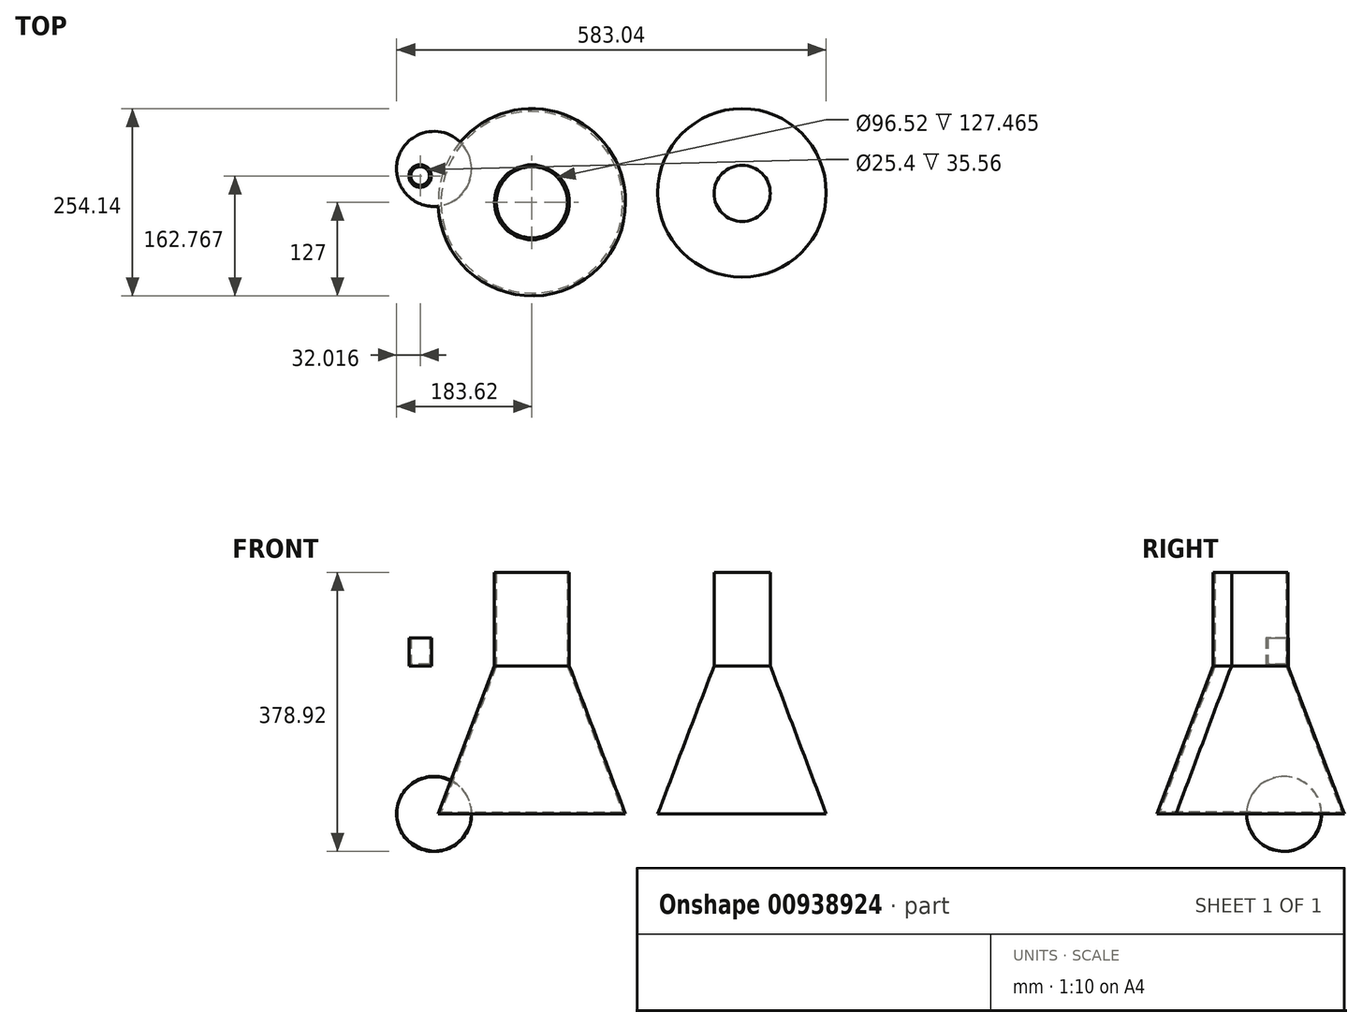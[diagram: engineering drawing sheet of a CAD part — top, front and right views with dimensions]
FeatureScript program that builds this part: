
annotation { "Feature Type Name" : "Feature", "Feature Type Description" : "" }
export const myFeature = defineFeature(function(context is Context, id is Id, definition is map)
    precondition{}
    {
        {
            var Q0;
            Q0=qCreatedBy(makeId("Top.planeOp"),FACE);
            var sketch = newSketch(context, id + "F0", { "sketchPlane" : qUnion([Q0])});
            skCircle(sketch, "E0", {"center": v(0, 0) * mm, "radius": 127 * mm});
            skSolve(sketch);
        }
        {
            var Q0;
            Q0=qCreatedBy(makeId("Top.planeOp"),FACE);
            cPlane(context, id + "F1", {"entities" : qUnion([Q0]), "cplaneType" : CPlaneType.OFFSET, "offset" : 200.9 * mm, "width" : 152.4 * mm, "height" : 152.4 * mm});
        }
        {
            var Q0;
            Q0=qCreatedBy(id+"F1.planeOp",FACE);
            var sketch = newSketch(context, id + "F2", { "sketchPlane" : qUnion([Q0])});
            skCircle(sketch, "E1", {"center": v(0, 0) * mm, "radius": 50.8 * mm});
            skSolve(sketch);
        }
        {
            var Q0;
            Q0=makeQuery(id+"F2.imprint","IMPRINT",FACE,{"disambiguationData":[TD([[makeQuery(id+"F2.imprint","IMPRINT",EDGE,{"derivedFrom":sQuery(id+"F2.wireOp",EDGE,"E1")}),1.0]])]});
            var sketch = newSketch(context, id + "F3", { "sketchPlane" : qUnion([Q0])});
            skCircle(sketch, "E2", {"center": v(0, 0) * mm, "radius": 19.15 * mm});
            skSolve(sketch);
        }
        {
            var Q0;
            Q0=makeQuery(id+"F0.imprint","IMPRINT",FACE,{"disambiguationData":[TD([[makeQuery(id+"F0.imprint","IMPRINT",EDGE,{"derivedFrom":sQuery(id+"F0.wireOp",EDGE,"E0")}),1.0]])]});
            var Q1;
            Q1=makeQuery(id+"F2.imprint","IMPRINT",FACE,{"disambiguationData":[TD([[makeQuery(id+"F2.imprint","IMPRINT",EDGE,{"derivedFrom":sQuery(id+"F2.wireOp",EDGE,"E1")}),1.0]])]});
            loft(context, id + "F4", {"sheetProfilesArray" : [{ "sheetProfileEntities" : qUnion([Q0]) }, { "sheetProfileEntities" : qUnion([Q1]) }]});
        }
        {
            var Q0;
            Q0=makeQuery(id+"F3.imprint","IMPRINT",FACE,{"disambiguationData":[TD([[makeQuery(id+"F3.imprint","IMPRINT",EDGE,{"derivedFrom":sQuery(id+"F3.wireOp",EDGE,"E2")}),-1.0]])]});
            var Q1;
            Q1=makeQuery(id+"F2.imprint","IMPRINT",FACE,{"disambiguationData":[TD([[makeQuery(id+"F2.imprint","IMPRINT",EDGE,{"derivedFrom":sQuery(id+"F2.wireOp",EDGE,"E1")}),1.0]])]});
            extrude(context, id + "F5", {"entities" : qUnion([Q0, Q1]), "operationType" : NewBodyOperationType.ADD, "depth" : 127 * mm, "offsetDistance" : 25.4 * mm});
        }
        {
            var Q0;
            Q0=qCreatedBy(makeId("Top.planeOp"),FACE);
            var sketch = newSketch(context, id + "F6", { "sketchPlane" : qUnion([Q0])});
            skArc(sketch, "E3", {"start": v(-89.56, 72.06) * mm, "mid": v(-159.63, 88.57) * mm, "end": v(-175.86, 18.43) * mm});
            skLineSegment(sketch, "E4", {"start": v(-89.56, 72.06) * mm, "end": v(-175.86, 18.43) * mm});
            skSolve(sketch);
        }
        {
            var Q0;
            Q0=makeQuery(id+"F6.imprint","IMPRINT",FACE,{"disambiguationData":[TD([[makeQuery(id+"F6.imprint","IMPRINT",EDGE,{"derivedFrom":sQuery(id+"F6.wireOp",EDGE,"E3")}),1.0]])]});
            var Q1;
            Q1=sQuery(id+"F6.wireOp",EDGE,"E4");
            revolve(context, id + "F7", {"surfaceOperationType" : NewSurfaceOperationType.NEW, "entities" : qUnion([Q0]), "axis" : qUnion([Q1]), "revolveType" : RevolveType.FULL});
        }
        {
            var Q0;
            Q0=qCreatedBy(id+"F1.planeOp",FACE);
            var sketch = newSketch(context, id + "F8", { "sketchPlane" : qUnion([Q0])});
            skCircle(sketch, "E5", {"center": v(-151.6, 35.77) * mm, "radius": 15.24 * mm});
            skSolve(sketch);
        }
        {
            var Q0;
            Q0=makeQuery(id+"F8.imprint","IMPRINT",FACE,{"disambiguationData":[TD([[makeQuery(id+"F8.imprint","IMPRINT",EDGE,{"derivedFrom":sQuery(id+"F8.wireOp",EDGE,"E5")}),1.0]])]});
            extrude(context, id + "F9", {"entities" : qUnion([Q0]), "depth" : 38.1 * mm, "offsetDistance" : 25.4 * mm});
        }
        {
            var Q0;
            Q0=makeQuery(id+"F5.opExtrude","CAP_FACE",FACE,{"disambiguationData":[OSD([sQuery(id+"F2.wireOp",EDGE,"E1")])],"isStart":false});
            shell(context, id + "F10", {"entities" : qUnion([Q0]), "thickness" : 2.54 * mm});
        }
        {
            var Q0;
            Q0=makeQuery(id+"F9.opExtrude","CAP_FACE",FACE,{"disambiguationData":[OSD([sQuery(id+"F8.wireOp",EDGE,"E5")])],"isStart":false});
            shell(context, id + "F11", {"entities" : qUnion([Q0]), "thickness" : 2.54 * mm});
        }
        {
            var Q0;
            Q0=makeQuery(id+"F0.imprint","IMPRINT",FACE,{"disambiguationData":[TD([[makeQuery(id+"F0.imprint","IMPRINT",EDGE,{"derivedFrom":sQuery(id+"F0.wireOp",EDGE,"E0")}),1.0]])]});
            var sketch = newSketch(context, id + "F12", { "sketchPlane" : qUnion([Q0])});
            skCircle(sketch, "E6", {"center": v(285.12, 12.84) * mm, "radius": 114.3 * mm});
            skSolve(sketch);
        }
        {
            var Q0;
            Q0=qCreatedBy(id+"F1.planeOp",FACE);
            var sketch = newSketch(context, id + "F13", { "sketchPlane" : qUnion([Q0])});
            skCircle(sketch, "E7", {"center": v(285.41, 12.13) * mm, "radius": 38.1 * mm});
            skSolve(sketch);
        }
        {
            var Q0;
            Q0=makeQuery(id+"F12.imprint","IMPRINT",FACE,{"disambiguationData":[TD([[makeQuery(id+"F12.imprint","IMPRINT",EDGE,{"derivedFrom":sQuery(id+"F12.wireOp",EDGE,"E6")}),1.0]])]});
            var Q1;
            Q1=makeQuery(id+"F13.imprint","IMPRINT",FACE,{"disambiguationData":[TD([[makeQuery(id+"F13.imprint","IMPRINT",EDGE,{"derivedFrom":sQuery(id+"F13.wireOp",EDGE,"E7")}),1.0]])]});
            loft(context, id + "F14", {"sheetProfilesArray" : [{ "sheetProfileEntities" : qUnion([Q0]) }, { "sheetProfileEntities" : qUnion([Q1]) }]});
        }
        {
            var Q0;
            Q0=makeQuery(id+"F14.opLoft","CAP_FACE",FACE,{"disambiguationData":[OSD([makeQuery(id+"F13.imprint","IMPRINT",FACE,{"disambiguationData":[TD([[makeQuery(id+"F13.imprint","IMPRINT",EDGE,{"derivedFrom":sQuery(id+"F13.wireOp",EDGE,"E7")}),1.0]])]})])],"isStart":true});
            extrude(context, id + "F15", {"entities" : qUnion([Q0]), "operationType" : NewBodyOperationType.ADD, "depth" : 127 * mm, "offsetDistance" : 25.4 * mm});
        }
    });
